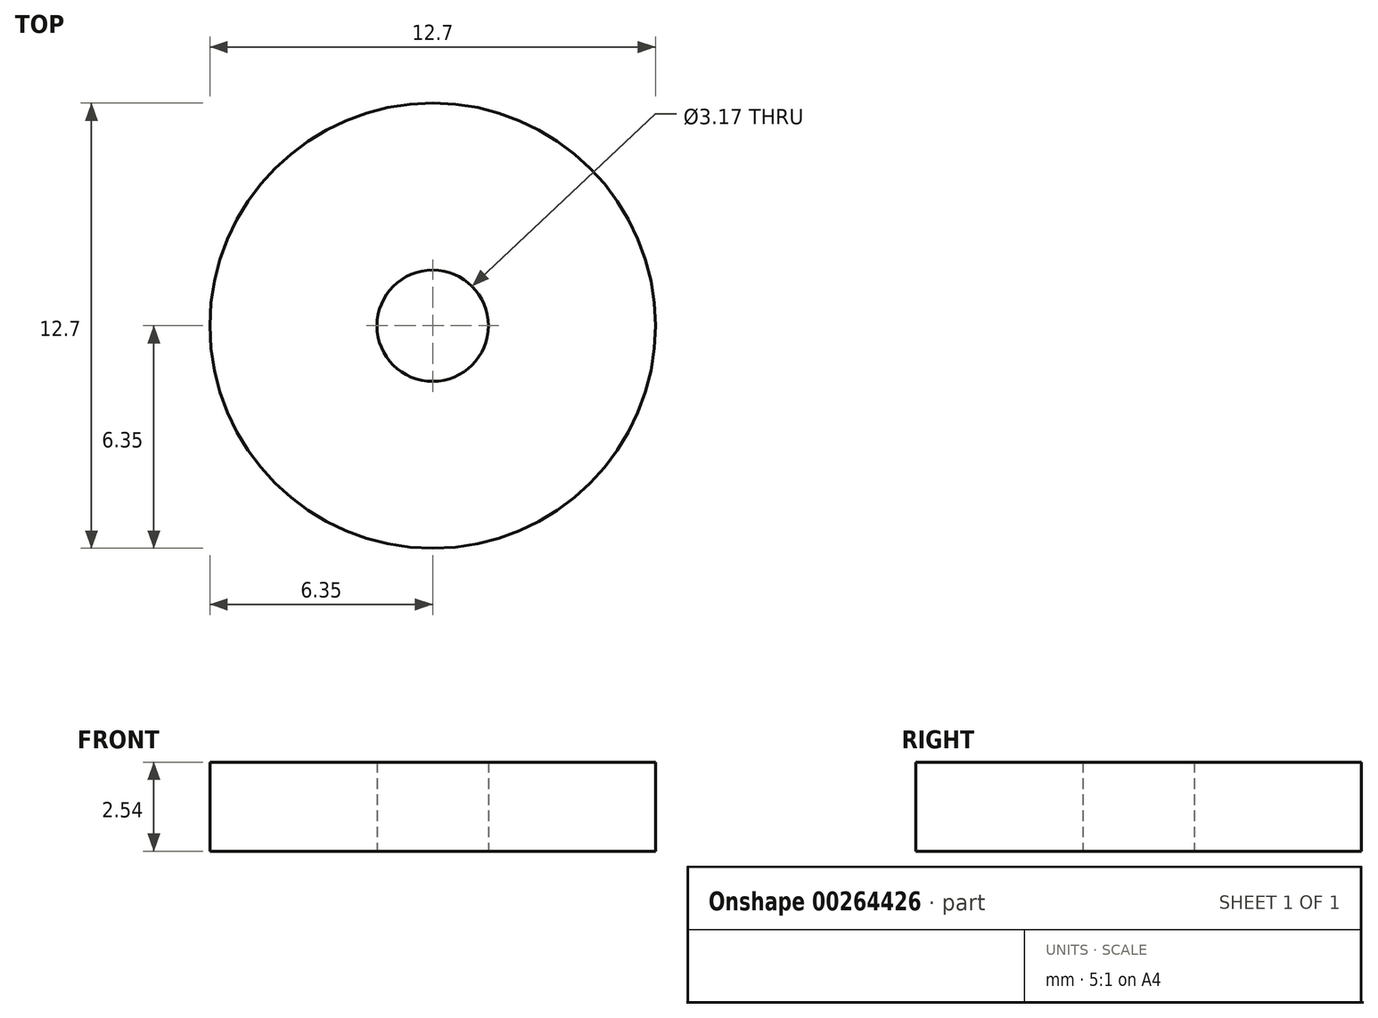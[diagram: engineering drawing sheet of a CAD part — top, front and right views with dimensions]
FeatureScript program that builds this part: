
annotation { "Feature Type Name" : "Feature", "Feature Type Description" : "" }
export const myFeature = defineFeature(function(context is Context, id is Id, definition is map)
    precondition{}
    {
        {
            var Q0;
            Q0=qCreatedBy(makeId("Top.planeOp"),FACE);
            var sketch = newSketch(context, id + "F0", { "sketchPlane" : qUnion([Q0])});
            skCircle(sketch, "E0", {"center": v(0, 0) * mm, "radius": 6.35 * mm});
            skCircle(sketch, "E1", {"center": v(0, 0) * mm, "radius": 1.59 * mm});
            skSolve(sketch);
        }
        {
            var Q0;
            Q0 = qSketchRegion(id + "F0", true);
            extrude(context, id + "F1", {"entities" : qUnion([Q0]), "depth" : 2.54 * mm});
        }
    });
